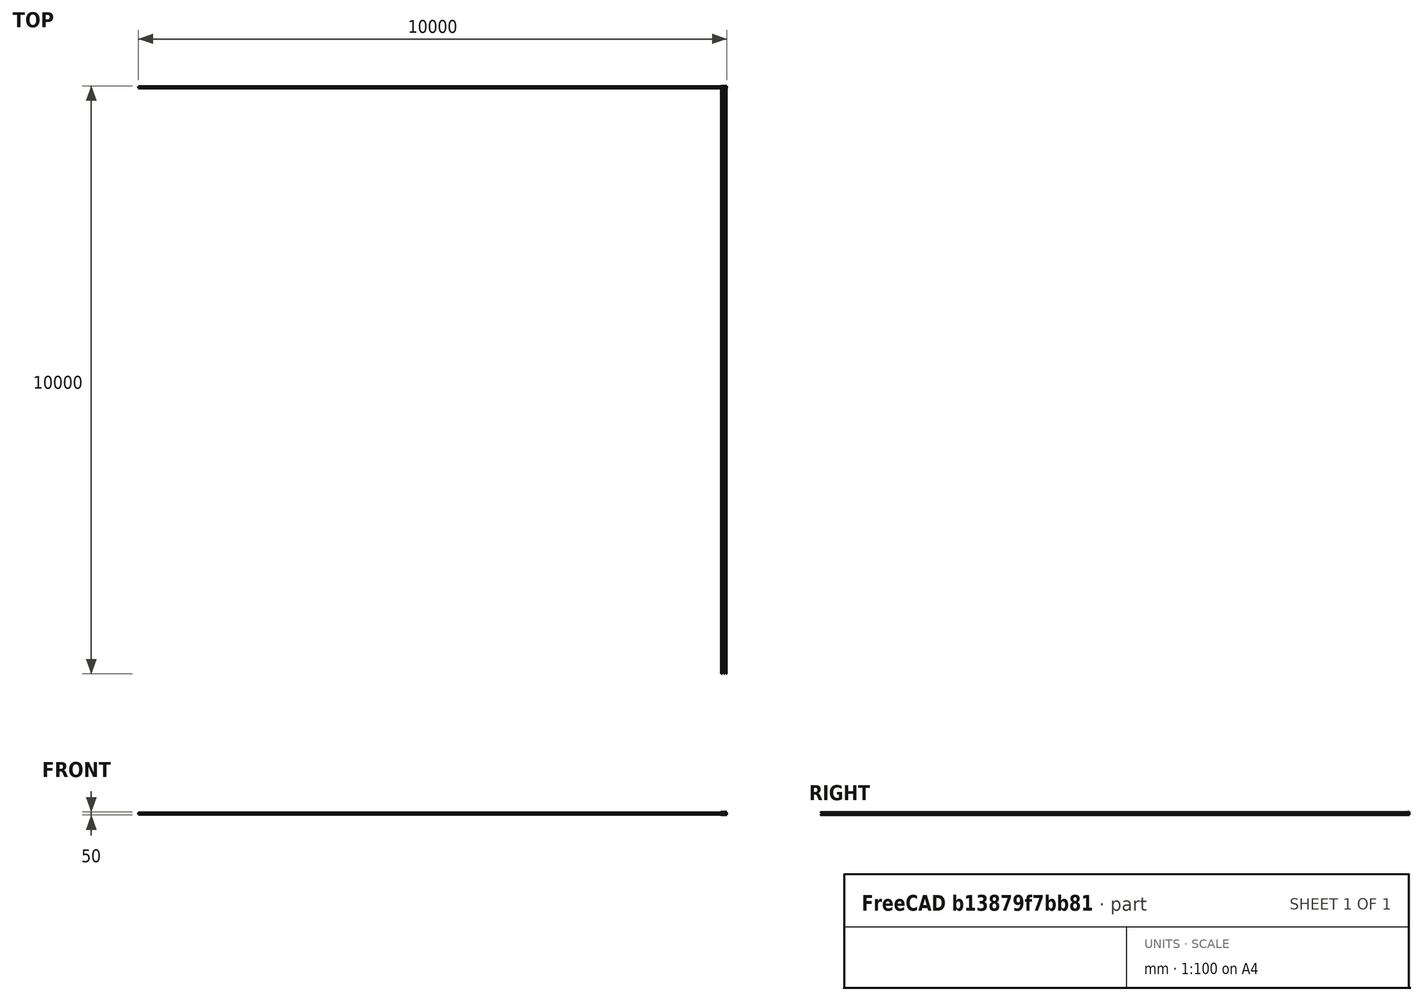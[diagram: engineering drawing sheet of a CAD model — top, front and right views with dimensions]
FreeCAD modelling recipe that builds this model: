
FCSTD DOCUMENT  (FreeCAD 0.16R)
Label: TubeHolderCap
License: All rights reserved
LicenseURL: http://en.wikipedia.org/wiki/All_rights_reserved
objects: Sketcher::SketchObject×3, PartDesign::Pocket×2, PartDesign::Pad×1, Mesh::Feature×1
note: 9 computed .brp shape members not serialized (recipe doc carries the construction recipe); baked Part::Feature solids carry a one-line shape summary decoded from their .brp

FEATURE [Sketcher::SketchObject] Sketch
  sketch-geometry (4):
    g0: LineSegment StartX=-50 StartY=0 StartZ=0 EndX=50 EndY=0 EndZ=0
    g1: LineSegment StartX=50 StartY=0 StartZ=0 EndX=50 EndY=-25 EndZ=0
    g2: LineSegment StartX=50 StartY=-25 StartZ=0 EndX=-50 EndY=-25 EndZ=0
    g3: LineSegment StartX=-50 StartY=-25 StartZ=0 EndX=-50 EndY=0 EndZ=0
  constraints (12):
    c: Horizontal(g0)
    c: Vertical(g1)
    c: Coincident(g1,g2)
    c: Horizontal(g2)
    c: Coincident(g2,g3)
    c: PointOnObject(g-1,g0)
    c: Symmetric(g0,g0,g-1)
    c: Vertical(g3)
    c: DistanceY(g1) = -25
    c: Symmetric(g1,g3,g-2)
    c: Distance(g3,g1) = 100
    c: Coincident(g0,g1)
FEATURE [PartDesign::Pad] Pad
  Length = 50
  Length2 = 100
  Sketch = -> Sketch
  Type = 0
FEATURE [Sketcher::SketchObject] Sketch003
  ExternalGeometry = -> [Pad]
  Placement = pos=(50,0,0) rot=(0.57735,0.57735,0.57735;2.0944rad)
  Support = -> Pad [Face2]
  sketch-geometry (1):
    g0: Circle CenterX=-25 CenterY=25 CenterZ=0 NormalX=0 NormalY=0 NormalZ=1 Radius=14.3
  constraints (2):
    c: Radius(g0) = 14.3
    c: Symmetric(g-4,g-5,g0)
FEATURE [PartDesign::Pocket] Pocket
  Length = 5
  Sketch = -> Sketch003
  Type = 1
FEATURE [Sketcher::SketchObject] Sketch002
  Placement = pos=(0,0,0) rot=(0,0.707107,0.707107;3.14159rad)
  Support = -> Pocket [Face1]
  sketch-geometry (8):
    g0: Circle CenterX=-40 CenterY=44.9849 CenterZ=0 NormalX=0 NormalY=0 NormalZ=1 Radius=2.8
    g1: Circle CenterX=0 CenterY=44.9849 CenterZ=0 NormalX=0 NormalY=0 NormalZ=1 Radius=2.8
    g2: Circle CenterX=40 CenterY=44.9849 CenterZ=0 NormalX=0 NormalY=0 NormalZ=1 Radius=2.8
    g3: Circle CenterX=-40 CenterY=4.42858 CenterZ=0 NormalX=0 NormalY=0 NormalZ=1 Radius=2.8
    g4: Circle CenterX=0 CenterY=4.42858 CenterZ=0 NormalX=0 NormalY=0 NormalZ=1 Radius=2.8
    g5: Circle CenterX=40 CenterY=4.42858 CenterZ=0 NormalX=0 NormalY=0 NormalZ=1 Radius=2.8
    g6: LineSegment [constr] StartX=-50 StartY=44.9849 StartZ=0 EndX=50 EndY=44.9849 EndZ=0
    g7: LineSegment [constr] StartX=-50 StartY=4.42858 StartZ=0 EndX=50 EndY=4.42858 EndZ=0
  constraints (20):
    c: Radius(g2) = 2.8
    c: Equal(g2,g1)
    c: Equal(g2,g0)
    c: Equal(g2,g3)
    c: Equal(g2,g4)
    c: Equal(g2,g5)
    c: Horizontal(g6)
    c: Horizontal(g7)
    c: PointOnObject(g3,g7)
    c: PointOnObject(g4,g7)
    c: PointOnObject(g5,g7)
    c: PointOnObject(g2,g6)
    c: PointOnObject(g1,g6)
    c: PointOnObject(g0,g6)
    c: DistanceX(g2) = 40
    c: DistanceX(g0) = -40
    c: DistanceX(g3) = -40
    c: DistanceX(g5) = 40
    c: PointOnObject(g1,g-2)
    c: PointOnObject(g4,g-2)
FEATURE [PartDesign::Pocket] Pocket001
  Length = 5
  Sketch = -> Sketch002
  Type = 1
FEATURE [Mesh::Feature] Mesh  label="Pocket001 (Meshed)"
